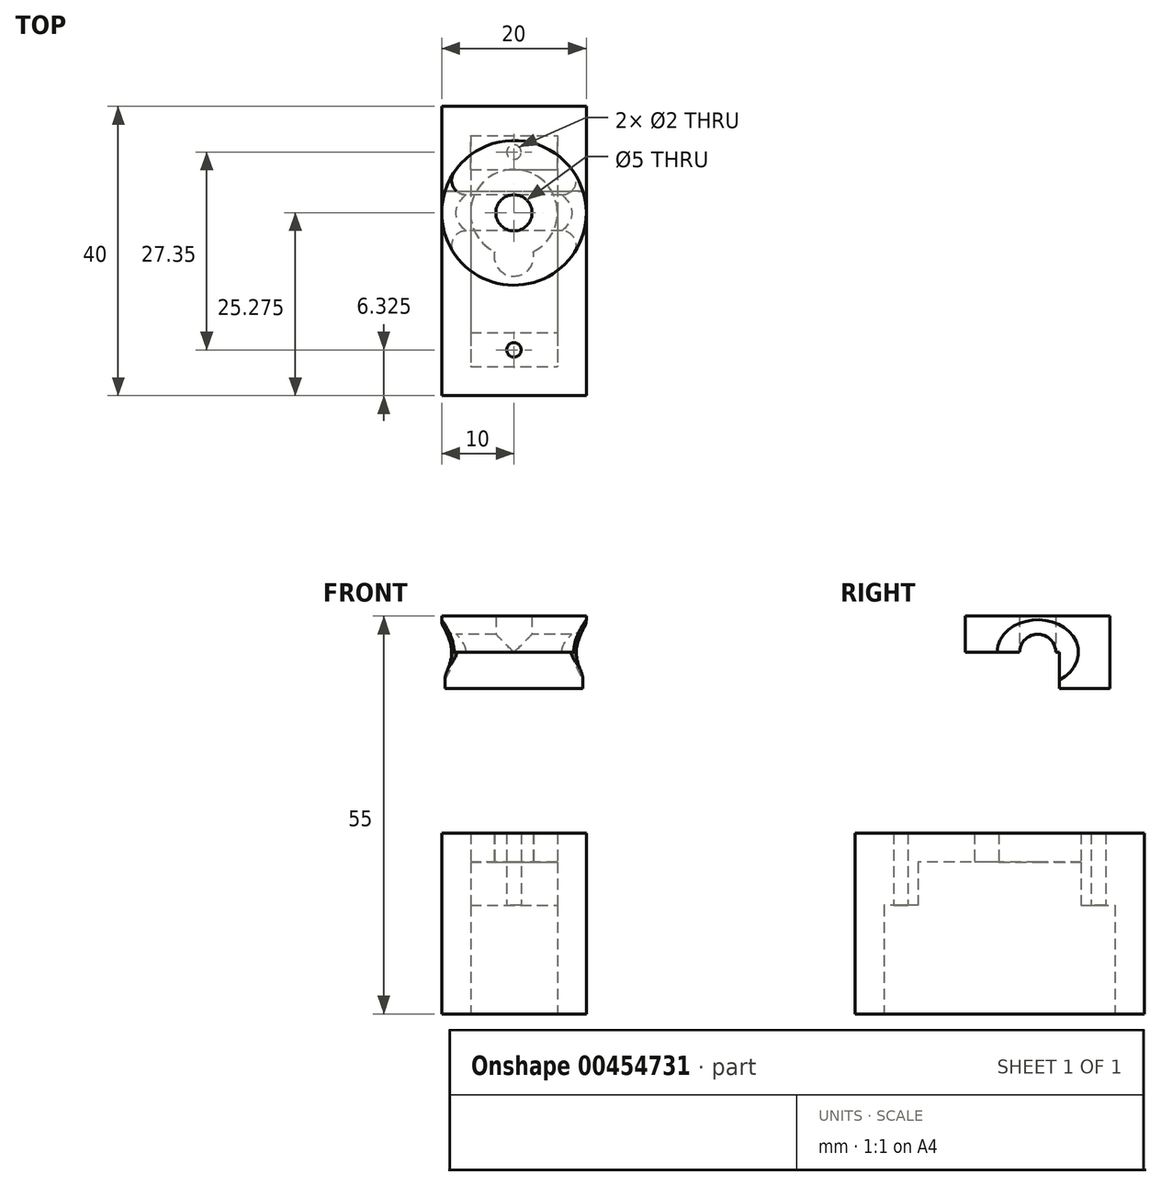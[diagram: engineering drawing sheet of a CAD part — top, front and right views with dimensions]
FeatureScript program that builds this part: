
annotation { "Feature Type Name" : "Feature", "Feature Type Description" : "" }
export const myFeature = defineFeature(function(context is Context, id is Id, definition is map)
    precondition{}
    {
        {
            var Q0;
            Q0=qCreatedBy(makeId("Top.planeOp"),FACE);
            var sketch = newSketch(context, id + "F0", { "sketchPlane" : qUnion([Q0])});
            skLineSegment(sketch, "E0.bottom", {"start": v(10, -20) * mm, "end": v(-10, -20) * mm});
            skLineSegment(sketch, "E0.top", {"start": v(10, 20) * mm, "end": v(-10, 20) * mm});
            skLineSegment(sketch, "E0.left", {"start": v(10, -20) * mm, "end": v(10, 20) * mm});
            skLineSegment(sketch, "E0.right", {"start": v(-10, -20) * mm, "end": v(-10, 20) * mm});
            skPoint(sketch, "E0.middle", {"position": v(0, 0) * mm});
            skLineSegment(sketch, "E1.bottom", {"start": v(-6, 11.28) * mm, "end": v(6, 11.28) * mm});
            skLineSegment(sketch, "E1.top", {"start": v(-6, -11.28) * mm, "end": v(6, -11.28) * mm});
            skLineSegment(sketch, "E1.left", {"start": v(-6, 11.28) * mm, "end": v(-6, -11.28) * mm});
            skLineSegment(sketch, "E1.right", {"start": v(6, 11.28) * mm, "end": v(6, -11.28) * mm});
            skCircle(sketch, "E2", {"center": v(0, -13.67) * mm, "radius": 1 * mm});
            skCircle(sketch, "E3", {"center": v(0, -0.73) * mm, "radius": 2.75 * mm});
            skCircle(sketch, "E4", {"center": v(0, 5.27) * mm, "radius": 6 * mm});
            skLineSegment(sketch, "E5.top", {"start": v(-6, -15.97) * mm, "end": v(6, -15.97) * mm});
            skLineSegment(sketch, "E5.left", {"start": v(-6, -11.28) * mm, "end": v(-6, -15.97) * mm});
            skLineSegment(sketch, "E5.right", {"start": v(6, -11.28) * mm, "end": v(6, -15.97) * mm});
            skLineSegment(sketch, "E6", {"start": v(0.7, -14.39) * mm, "end": v(0.7, -15.97) * mm});
            skLineSegment(sketch, "E7.MirrorCS", {"start": v(-0.7, -14.39) * mm, "end": v(-0.7, -15.97) * mm});
            skLineSegment(sketch, "E8.MirrorCS", {"start": v(-6, 15.98) * mm, "end": v(6, 15.98) * mm});
            skLineSegment(sketch, "E9.MirrorCS", {"start": v(-6, 11.28) * mm, "end": v(-6, 15.98) * mm});
            skLineSegment(sketch, "E10.MirrorCS", {"start": v(6, 11.28) * mm, "end": v(6, 15.98) * mm});
            skCircle(sketch, "E11.MirrorC", {"center": v(0, 13.67) * mm, "radius": 1 * mm});
            skLineSegment(sketch, "E12.MirrorCS", {"start": v(0.7, 14.39) * mm, "end": v(0.7, 15.97) * mm});
            skLineSegment(sketch, "E13.MirrorCS", {"start": v(-0.7, 14.39) * mm, "end": v(-0.7, 15.97) * mm});
            skSolve(sketch);
        }
        {
            var Q0;
            Q0=makeQuery(id+"F0.imprint","IMPRINT",FACE,{"disambiguationData":[TD([[makeQuery(id+"F0.imprint","IMPRINT",EDGE,{"derivedFrom":sQuery(id+"F0.wireOp",EDGE,"E0.bottom")}),-1.0]])]});
            var Q1;
            {var subQ0=sQuery(id+"F0.wireOp",EDGE,"E9.MirrorCS");Q1=makeQuery(id+"F0.imprint","IMPRINT",FACE,{"disambiguationData":[TD([[makeQuery(id+"F0.imprint","IMPRINT",EDGE,{"derivedFrom":subQ0}),-1.0]])]});}
            var Q2;
            {var subQ1=sQuery(id+"F0.wireOp",EDGE,"E1.bottom");var subQ3=sQuery(id+"F0.wireOp",EDGE,"E4");var subQ4=makeQuery(id+"F0.imprint","INTERSECT",VERTEX,{"derivedFrom":[subQ1,subQ3]});Q2=makeQuery(id+"F0.imprint","IMPRINT",FACE,{"disambiguationData":[TD([[makeQuery(id+"F0.imprint","IMPRINT",EDGE,{"disambiguationData":[TD([[subQ4,-1.0]])],"derivedFrom":subQ3}),-1.0]])]});}
            var Q3;
            {var subQ1=sQuery(id+"F0.wireOp",EDGE,"E1.bottom");var subQ3=sQuery(id+"F0.wireOp",EDGE,"E4");var subQ4=makeQuery(id+"F0.imprint","INTERSECT",VERTEX,{"derivedFrom":[subQ1,subQ3]});Q3=makeQuery(id+"F0.imprint","IMPRINT",FACE,{"disambiguationData":[TD([[makeQuery(id+"F0.imprint","IMPRINT",EDGE,{"disambiguationData":[TD([[subQ4,1.0]])],"derivedFrom":subQ3}),-1.0]])]});}
            var Q4;
            {var subQ6=sQuery(id+"F0.wireOp",EDGE,"E1.top");Q4=makeQuery(id+"F0.imprint","IMPRINT",FACE,{"disambiguationData":[TD([[makeQuery(id+"F0.imprint","IMPRINT",EDGE,{"derivedFrom":subQ6}),1.0]])]});}
            var Q5;
            Q5=makeQuery(id+"F0.imprint","IMPRINT",FACE,{"disambiguationData":[TD([[makeQuery(id+"F0.imprint","IMPRINT",EDGE,{"derivedFrom":sQuery(id+"F0.wireOp",EDGE,"E1.top")}),-1.0]])]});
            var Q6;
            {var subQ0=sQuery(id+"F0.wireOp",EDGE,"E6");Q6=makeQuery(id+"F0.imprint","IMPRINT",FACE,{"disambiguationData":[TD([[makeQuery(id+"F0.imprint","IMPRINT",EDGE,{"derivedFrom":subQ0}),-1.0]])]});}
            var Q7;
            {var subQ0=sQuery(id+"F0.wireOp",EDGE,"E12.MirrorCS");Q7=makeQuery(id+"F0.imprint","IMPRINT",FACE,{"disambiguationData":[TD([[makeQuery(id+"F0.imprint","IMPRINT",EDGE,{"derivedFrom":subQ0}),1.0]])]});}
            extrude(context, id + "F1", {"entities" : qUnion([Q0, Q1, Q2, Q3, Q4, Q5, Q6, Q7]), "depth" : 25 * mm});
        }
        {
            var Q0;
            {var subQ6=sQuery(id+"F0.wireOp",EDGE,"E1.top");Q0=makeQuery(id+"F0.imprint","IMPRINT",FACE,{"disambiguationData":[TD([[makeQuery(id+"F0.imprint","IMPRINT",EDGE,{"derivedFrom":subQ6}),1.0]])]});}
            var Q1;
            {var subQ1=sQuery(id+"F0.wireOp",EDGE,"E1.bottom");var subQ3=sQuery(id+"F0.wireOp",EDGE,"E4");var subQ4=makeQuery(id+"F0.imprint","INTERSECT",VERTEX,{"derivedFrom":[subQ1,subQ3]});Q1=makeQuery(id+"F0.imprint","IMPRINT",FACE,{"disambiguationData":[TD([[makeQuery(id+"F0.imprint","IMPRINT",EDGE,{"disambiguationData":[TD([[subQ4,1.0]])],"derivedFrom":subQ3}),-1.0]])]});}
            var Q2;
            {var subQ1=sQuery(id+"F0.wireOp",EDGE,"E1.bottom");var subQ3=sQuery(id+"F0.wireOp",EDGE,"E4");var subQ4=makeQuery(id+"F0.imprint","INTERSECT",VERTEX,{"derivedFrom":[subQ1,subQ3]});Q2=makeQuery(id+"F0.imprint","IMPRINT",FACE,{"disambiguationData":[TD([[makeQuery(id+"F0.imprint","IMPRINT",EDGE,{"disambiguationData":[TD([[subQ4,-1.0]])],"derivedFrom":subQ3}),-1.0]])]});}
            extrude(context, id + "F2", {"entities" : qUnion([Q0, Q1, Q2]), "operationType" : NewBodyOperationType.REMOVE, "depth" : 21 * mm});
        }
        {
            var Q0;
            {var subQ0=sQuery(id+"F0.wireOp",EDGE,"E9.MirrorCS");Q0=makeQuery(id+"F0.imprint","IMPRINT",FACE,{"disambiguationData":[TD([[makeQuery(id+"F0.imprint","IMPRINT",EDGE,{"derivedFrom":subQ0}),-1.0]])]});}
            var Q1;
            Q1=makeQuery(id+"F0.imprint","IMPRINT",FACE,{"disambiguationData":[TD([[makeQuery(id+"F0.imprint","IMPRINT",EDGE,{"derivedFrom":sQuery(id+"F0.wireOp",EDGE,"E1.top")}),-1.0]])]});
            var Q2;
            {var subQ0=sQuery(id+"F0.wireOp",EDGE,"E6");Q2=makeQuery(id+"F0.imprint","IMPRINT",FACE,{"disambiguationData":[TD([[makeQuery(id+"F0.imprint","IMPRINT",EDGE,{"derivedFrom":subQ0}),-1.0]])]});}
            var Q3;
            {var subQ0=sQuery(id+"F0.wireOp",EDGE,"E12.MirrorCS");Q3=makeQuery(id+"F0.imprint","IMPRINT",FACE,{"disambiguationData":[TD([[makeQuery(id+"F0.imprint","IMPRINT",EDGE,{"derivedFrom":subQ0}),1.0]])]});}
            extrude(context, id + "F3", {"entities" : qUnion([Q0, Q1, Q2, Q3]), "operationType" : NewBodyOperationType.REMOVE, "depth" : 15 * mm});
        }
        {
            var Q0;
            Q0=qCreatedBy(makeId("Top.planeOp"),FACE);
            cPlane(context, id + "F4", {"entities" : qUnion([Q0]), "cplaneType" : CPlaneType.OFFSET, "offset" : 50 * mm, "width" : 150 * mm, "height" : 150 * mm});
        }
        {
            var Q0;
            Q0=qCreatedBy(id+"F4.planeOp",FACE);
            var sketch = newSketch(context, id + "F5", { "sketchPlane" : qUnion([Q0])});
            skCircle(sketch, "E14", {"center": v(0, 5.27) * mm, "radius": 10 * mm});
            skLineSegment(sketch, "E15", {"start": v(-16.18, 5.27) * mm, "end": v(17.6, 5.27) * mm, "construction": true});
            skLineSegment(sketch, "E16", {"start": v(-9.54, 8.27) * mm, "end": v(9.54, 8.27) * mm});
            skLineSegment(sketch, "E17", {"start": v(10, 5.27) * mm, "end": v(-10, 5.27) * mm});
            skCircle(sketch, "E18", {"center": v(0, 5.27) * mm, "radius": 2.5 * mm});
            skSolve(sketch);
        }
        {
            var Q0;
            {var subQ0=sQuery(id+"F5.wireOp",EDGE,"E17");Q0=makeQuery(id+"F5.imprint","IMPRINT",FACE,{"disambiguationData":[TD([[makeQuery(id+"F5.imprint","IMPRINT",EDGE,{"derivedFrom":subQ0}),1.0]])]});}
            var Q1;
            {var subQ0=sQuery(id+"F5.wireOp",EDGE,"E16");Q1=makeQuery(id+"F5.imprint","IMPRINT",FACE,{"disambiguationData":[TD([[makeQuery(id+"F5.imprint","IMPRINT",EDGE,{"derivedFrom":subQ0}),-1.0]])]});}
            var Q2;
            {var subQ0=sQuery(id+"F5.wireOp",EDGE,"E16");Q2=makeQuery(id+"F5.imprint","IMPRINT",FACE,{"disambiguationData":[TD([[makeQuery(id+"F5.imprint","IMPRINT",EDGE,{"derivedFrom":subQ0}),1.0]])]});}
            var Q3;
            {var subQ0=sQuery(id+"F5.wireOp",EDGE,"E18");var subQ1=sQuery(id+"F5.wireOp",EDGE,"E17");var subQ2=makeQuery(id+"F5.imprint","INTERSECT",VERTEX,{"disambiguationData":[OD(0.0)],"derivedFrom":[subQ1,subQ0]});Q3=makeQuery(id+"F5.imprint","IMPRINT",FACE,{"disambiguationData":[TD([[makeQuery(id+"F5.imprint","IMPRINT",EDGE,{"disambiguationData":[TD([[subQ2,-1.0]])],"derivedFrom":subQ1}),-1.0]])]});}
            var Q4;
            {var subQ0=sQuery(id+"F5.wireOp",EDGE,"E18");var subQ1=sQuery(id+"F5.wireOp",EDGE,"E17");var subQ2=makeQuery(id+"F5.imprint","INTERSECT",VERTEX,{"disambiguationData":[OD(0.0)],"derivedFrom":[subQ1,subQ0]});Q4=makeQuery(id+"F5.imprint","IMPRINT",FACE,{"disambiguationData":[TD([[makeQuery(id+"F5.imprint","IMPRINT",EDGE,{"disambiguationData":[TD([[subQ2,-1.0]])],"derivedFrom":subQ1}),1.0]])]});}
            extrude(context, id + "F6", {"entities" : qUnion([Q0, Q1, Q2, Q3, Q4]), "depth" : 5 * mm, "hasSecondDirection" : true, "secondDirectionOppositeDirection" : true, "secondDirectionDepth" : 5 * mm});
        }
        {
            var Q0;
            Q0=sQuery(id+"F5.wireOp",VERTEX,"E17.end");
            var Q1;
            Q1=sQuery(id+"F5.wireOp",EDGE,"E15");
            cPlane(context, id + "F7", {"entities" : qUnion([Q0, Q1]), "cplaneType" : CPlaneType.LINE_POINT, "offset" : 25 * mm, "width" : 150 * mm, "height" : 150 * mm});
        }
        {
            var Q0;
            Q0=qCreatedBy(id+"F7.planeOp",FACE);
            var sketch = newSketch(context, id + "F8", { "sketchPlane" : qUnion([Q0])});
            skCircle(sketch, "E19", {"center": v(5.27, 50) * mm, "radius": 2.5 * mm});
            skSolve(sketch);
        }
        {
            var Q0;
            Q0 = qSketchRegion(id + "F8", true);
            extrude(context, id + "F9", {"entities" : qUnion([Q0]), "operationType" : NewBodyOperationType.REMOVE, "endBound" : BoundingType.THROUGH_ALL, "depth" : 25 * mm});
        }
        {
            var Q0;
            {var subQ0=sQuery(id+"F5.wireOp",EDGE,"E18");var subQ1=sQuery(id+"F5.wireOp",EDGE,"E17");var subQ2=makeQuery(id+"F5.imprint","INTERSECT",VERTEX,{"disambiguationData":[OD(0.0)],"derivedFrom":[subQ1,subQ0]});Q0=makeQuery(id+"F5.imprint","IMPRINT",FACE,{"disambiguationData":[TD([[makeQuery(id+"F5.imprint","IMPRINT",EDGE,{"disambiguationData":[TD([[subQ2,-1.0]])],"derivedFrom":subQ1}),1.0]])]});}
            var Q1;
            {var subQ0=sQuery(id+"F5.wireOp",EDGE,"E18");var subQ1=sQuery(id+"F5.wireOp",EDGE,"E17");var subQ2=makeQuery(id+"F5.imprint","INTERSECT",VERTEX,{"disambiguationData":[OD(0.0)],"derivedFrom":[subQ1,subQ0]});Q1=makeQuery(id+"F5.imprint","IMPRINT",FACE,{"disambiguationData":[TD([[makeQuery(id+"F5.imprint","IMPRINT",EDGE,{"disambiguationData":[TD([[subQ2,-1.0]])],"derivedFrom":subQ1}),-1.0]])]});}
            var Q2;
            Q2=sQuery(id+"F5.wireOp",EDGE,"E18");
            extrude(context, id + "F10", {"entities" : qUnion([Q0, Q1]), "operationType" : NewBodyOperationType.REMOVE, "surfaceEntities" : qUnion([Q2]), "oppositeDirection" : true, "depth" : 5 * mm});
        }
        {
            var Q0;
            Q0=makeQuery(id+"F9.boolean.opBoolean","INTERSECT",EDGE,{"disambiguationData":[OD(0.0)],"derivedFrom":[makeQuery(id+"F6.opExtrude","SWEPT_FACE",FACE,{"disambiguationData":[OSD([sQuery(id+"F5.wireOp",EDGE,"E14")])]}),makeQuery(id+"F9.opExtrude","SWEPT_FACE",FACE,{"disambiguationData":[OSD([sQuery(id+"F8.wireOp",EDGE,"E19")])]})]});
            var Q1;
            Q1=makeQuery(id+"F9.boolean.opBoolean","INTERSECT",EDGE,{"disambiguationData":[OD(1.0)],"derivedFrom":[makeQuery(id+"F6.opExtrude","SWEPT_FACE",FACE,{"disambiguationData":[OSD([sQuery(id+"F5.wireOp",EDGE,"E14")])]}),makeQuery(id+"F9.opExtrude","SWEPT_FACE",FACE,{"disambiguationData":[OSD([sQuery(id+"F8.wireOp",EDGE,"E19")])]})]});
            fillet(context, id + "F11", {"entities" : qUnion([Q0, Q1]), "radius" : 2 * mm, "tangentPropagation" : true, "allowEdgeOverflow" : false});
        }
    });
